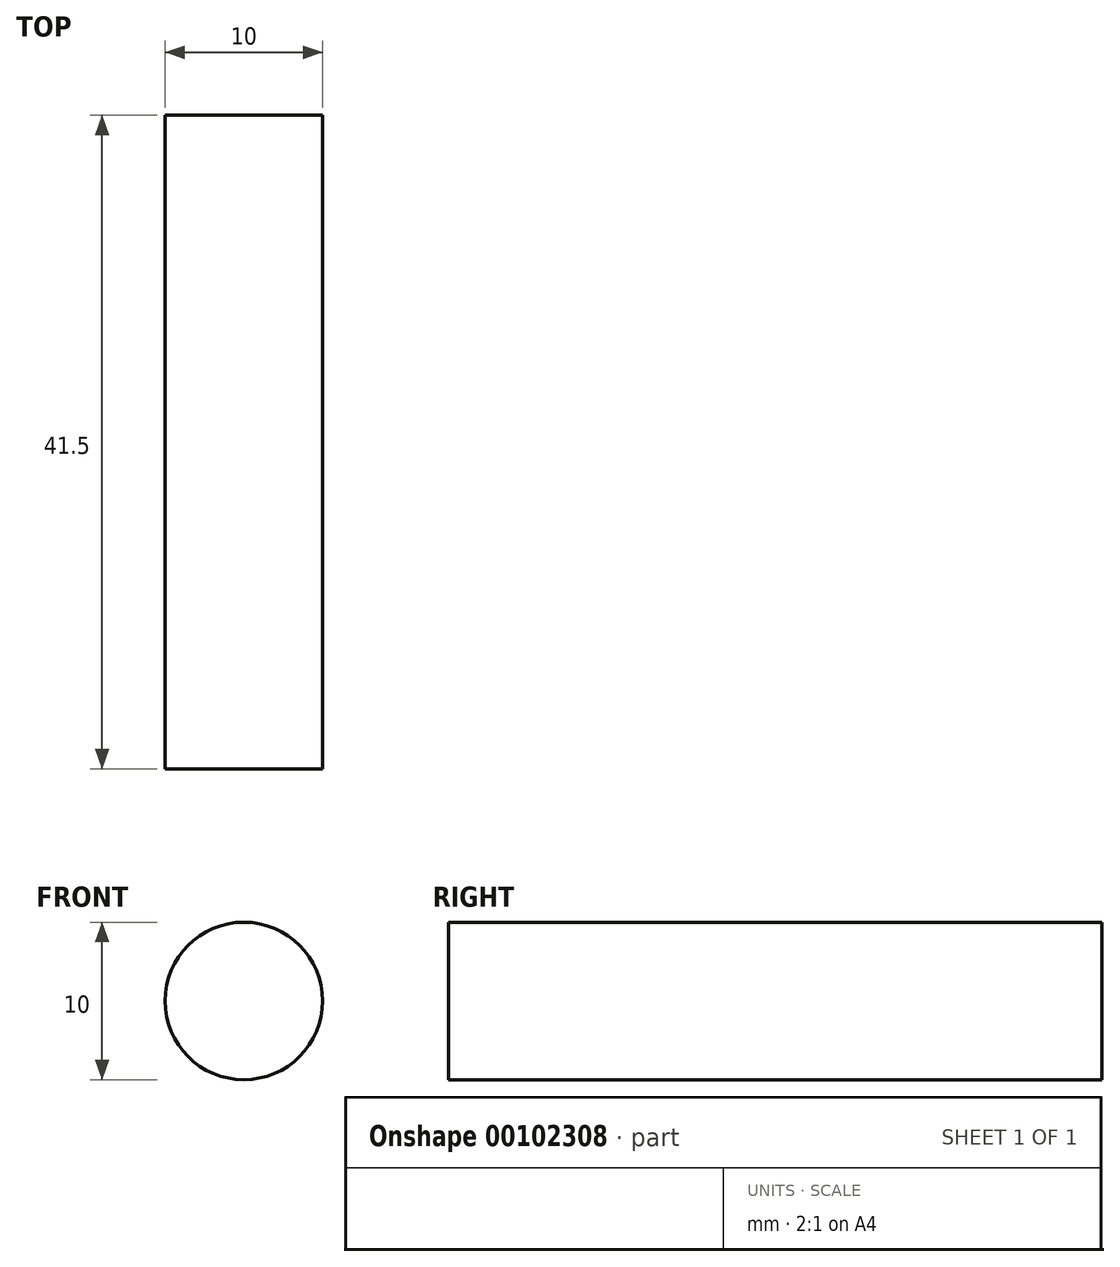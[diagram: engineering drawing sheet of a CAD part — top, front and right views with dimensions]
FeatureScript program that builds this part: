
annotation { "Feature Type Name" : "Feature", "Feature Type Description" : "" }
export const myFeature = defineFeature(function(context is Context, id is Id, definition is map)
    precondition{}
    {
        {
            var Q0;
            Q0=qCreatedBy(makeId("Front.planeOp"),FACE);
            var sketch = newSketch(context, id + "F0", { "sketchPlane" : qUnion([Q0])});
            skCircle(sketch, "E0", {"center": v(0, 0) * mm, "radius": 5 * mm});
            skSolve(sketch);
        }
        {
            var Q0;
            Q0=makeQuery(id+"F0.imprint","IMPRINT",FACE,{"disambiguationData":[TD([[makeQuery(id+"F0.imprint","IMPRINT",EDGE,{"derivedFrom":sQuery(id+"F0.wireOp",EDGE,"E0")}),1.0]])]});
            extrude(context, id + "F1", {"entities" : qUnion([Q0]), "oppositeDirection" : true, "depth" : 41.5 * mm, "symmetric" : true});
        }
    });
